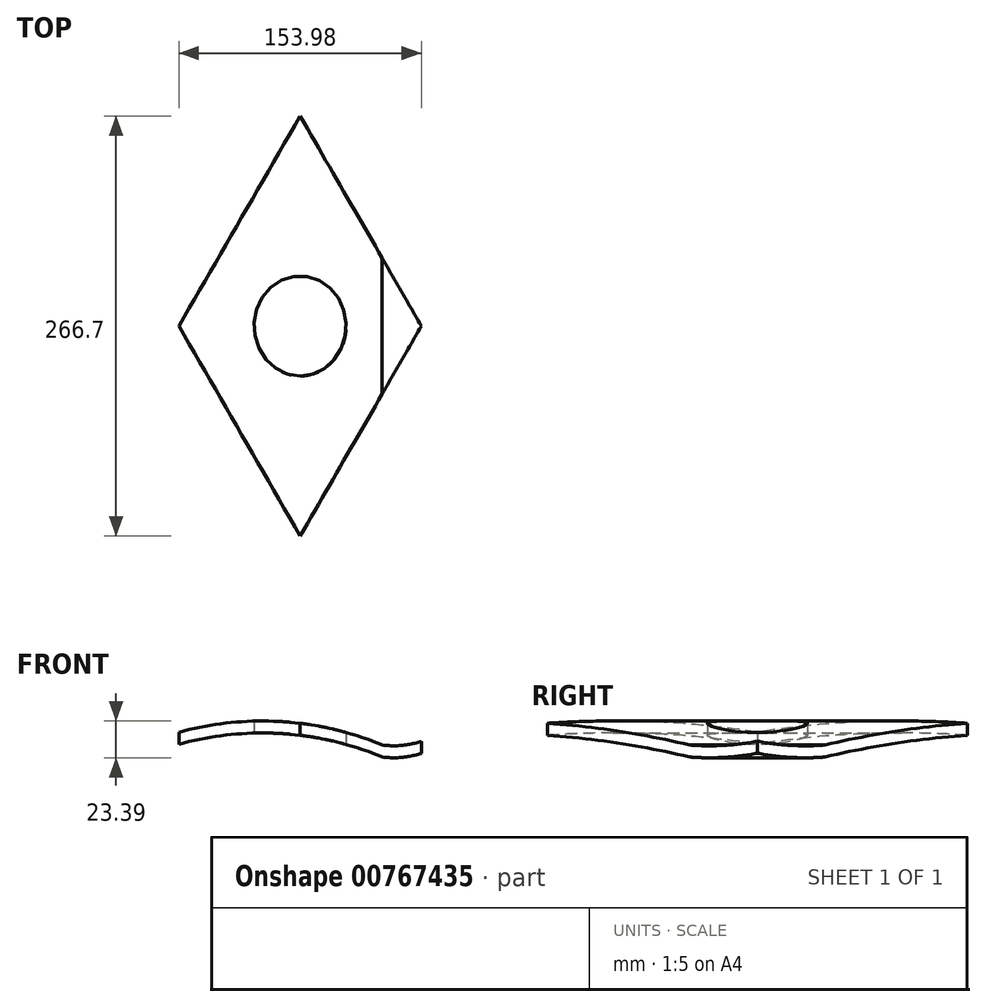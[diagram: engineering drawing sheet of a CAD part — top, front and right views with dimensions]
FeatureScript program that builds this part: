
annotation { "Feature Type Name" : "Feature", "Feature Type Description" : "" }
export const myFeature = defineFeature(function(context is Context, id is Id, definition is map)
    precondition{}
    {
        {
            var Q0;
            Q0=qCreatedBy(makeId("Front.planeOp"),FACE);
            var sketch = newSketch(context, id + "F0", { "sketchPlane" : qUnion([Q0])});
            skArc(sketch, "E0", {"start": v(22.86, 17.78) * mm, "mid": v(-53.34, 33.02) * mm, "end": v(-129.54, 17.78) * mm});
            skArc(sketch, "E1", {"start": v(22.86, 17.78) * mm, "mid": v(35.71, 17.52) * mm, "end": v(48.26, 20.32) * mm});
            skLineSegment(sketch, "E2", {"start": v(-129.54, 17.78) * mm, "end": v(-129.54, 0) * mm});
            skLineSegment(sketch, "E3", {"start": v(-129.54, 0) * mm, "end": v(48.26, 0) * mm});
            skLineSegment(sketch, "E4", {"start": v(48.26, 0) * mm, "end": v(48.26, 20.32) * mm});
            skLineSegment(sketch, "E5", {"start": v(0, 25.7) * mm, "end": v(0, 0) * mm});
            skLineSegment(sketch, "E6", {"start": v(-53.34, 33.02) * mm, "end": v(-53.34, 0) * mm});
            skLineSegment(sketch, "E7", {"start": v(35.71, 17.52) * mm, "end": v(35.71, 0) * mm});
            skArc(sketch, "E8", {"start": v(22.86, 25.4) * mm, "mid": v(35.71, 25.14) * mm, "end": v(48.26, 27.94) * mm});
            skArc(sketch, "E9", {"start": v(22.86, 25.4) * mm, "mid": v(-53.34, 40.64) * mm, "end": v(-129.54, 25.4) * mm});
            skLineSegment(sketch, "E10", {"start": v(48.26, 27.94) * mm, "end": v(48.26, 48.26) * mm});
            skLineSegment(sketch, "E11", {"start": v(48.26, 48.26) * mm, "end": v(-129.54, 48.26) * mm});
            skLineSegment(sketch, "E12", {"start": v(-129.54, 48.26) * mm, "end": v(-129.54, 25.4) * mm});
            skSolve(sketch);
        }
        {
            var Q0;
            Q0=makeQuery(id+"F0.imprint","IMPRINT",FACE,{"disambiguationData":[TD([[makeQuery(id+"F0.imprint","IMPRINT",EDGE,{"derivedFrom":sQuery(id+"F0.wireOp",EDGE,"E0")}),1.0]])]});
            var Q1;
            {var subQ1=sQuery(id+"F0.wireOp",EDGE,"E1");Q1=makeQuery(id+"F0.imprint","IMPRINT",FACE,{"disambiguationData":[TD([[makeQuery(id+"F0.imprint","IMPRINT",EDGE,{"derivedFrom":subQ1}),-1.0]])]});}
            var Q2;
            {var subQ0=sQuery(id+"F0.wireOp",EDGE,"E5");Q2=makeQuery(id+"F0.imprint","IMPRINT",FACE,{"disambiguationData":[TD([[makeQuery(id+"F0.imprint","IMPRINT",EDGE,{"derivedFrom":subQ0}),1.0]])]});}
            extrude(context, id + "F1", {"entities" : qUnion([Q0, Q1, Q2]), "depth" : 266.7 * mm, "offsetDistance" : 25.4 * mm});
        }
        {
            var Q0;
            Q0=makeQuery(id+"F0.imprint","IMPRINT",FACE,{"disambiguationData":[TD([[makeQuery(id+"F0.imprint","IMPRINT",EDGE,{"derivedFrom":sQuery(id+"F0.wireOp",EDGE,"E0")}),1.0]])]});
            extrude(context, id + "F2", {"entities" : qUnion([Q0]), "operationType" : NewBodyOperationType.ADD, "depth" : 266.7 * mm, "offsetDistance" : 25.4 * mm});
        }
        {
            var Q0;
            Q0=qCreatedBy(makeId("Top.planeOp"),FACE);
            var sketch = newSketch(context, id + "F3", { "sketchPlane" : qUnion([Q0])});
            skLineSegment(sketch, "E13", {"start": v(-29.2, 0) * mm, "end": v(47.78, -133.35) * mm});
            skLineSegment(sketch, "E14", {"start": v(-29.2, 0) * mm, "end": v(-106.2, -133.35) * mm});
            skLineSegment(sketch, "E15", {"start": v(-106.2, -133.35) * mm, "end": v(-29.2, -266.7) * mm});
            skLineSegment(sketch, "E16", {"start": v(47.78, -133.35) * mm, "end": v(-29.2, -266.7) * mm});
            skEllipse(sketch, "E17", {"center": v(-29.2, -133.35) * mm, "majorRadius": 31.75 * mm, "minorRadius": 29.21 * mm, "majorAxis": v(0, -1)});
            skSolve(sketch);
        }
        {
            var Q0;
            Q0=makeQuery(id+"F3.imprint","IMPRINT",FACE,{"disambiguationData":[TD([[makeQuery(id+"F3.imprint","IMPRINT",EDGE,{"derivedFrom":sQuery(id+"F3.wireOp",EDGE,"E13")}),-1.0]])]});
            extrude(context, id + "F4", {"entities" : qUnion([Q0]), "depth" : 42.67 * mm, "offsetDistance" : 25.4 * mm});
        }
        {
            var Q0;
            Q0=makeQuery(id+"F0.imprint","IMPRINT",FACE,{"disambiguationData":[TD([[makeQuery(id+"F0.imprint","IMPRINT",EDGE,{"derivedFrom":sQuery(id+"F0.wireOp",EDGE,"E8")}),1.0]])]});
            extrude(context, id + "F5", {"entities" : qUnion([Q0]), "depth" : 266.7 * mm, "offsetDistance" : 25.4 * mm});
        }
        {
            var Q0;
            Q0=makeQuery(id+"F1.opExtrude","SWEPT_BODY",BODY,{"disambiguationData":[OSD([sQuery(id+"F0.wireOp",EDGE,"E0"),sQuery(id+"F0.wireOp",EDGE,"E1"),sQuery(id+"F0.wireOp",EDGE,"E2"),sQuery(id+"F0.wireOp",EDGE,"E3"),sQuery(id+"F0.wireOp",EDGE,"E4")])]});
            var Q1;
            Q1=makeQuery(id+"F5.opExtrude","SWEPT_BODY",BODY,{"disambiguationData":[OSD([sQuery(id+"F0.wireOp",EDGE,"E8"),sQuery(id+"F0.wireOp",EDGE,"E9"),sQuery(id+"F0.wireOp",EDGE,"E10"),sQuery(id+"F0.wireOp",EDGE,"E11"),sQuery(id+"F0.wireOp",EDGE,"E12")])]});
            var Q2;
            Q2=makeQuery(id+"F4.opExtrude","SWEPT_BODY",BODY,{"disambiguationData":[OSD([sQuery(id+"F3.wireOp",EDGE,"E13"),sQuery(id+"F3.wireOp",EDGE,"E14"),sQuery(id+"F3.wireOp",EDGE,"E15"),sQuery(id+"F3.wireOp",EDGE,"E16"),sQuery(id+"F3.wireOp",EDGE,"E17")])]});
            booleanBodies(context, id + "F6", {"operationType" : BooleanOperationType.SUBTRACTION, "tools" : qUnion([Q0, Q1]), "targets" : qUnion([Q2])});
        }
    });
